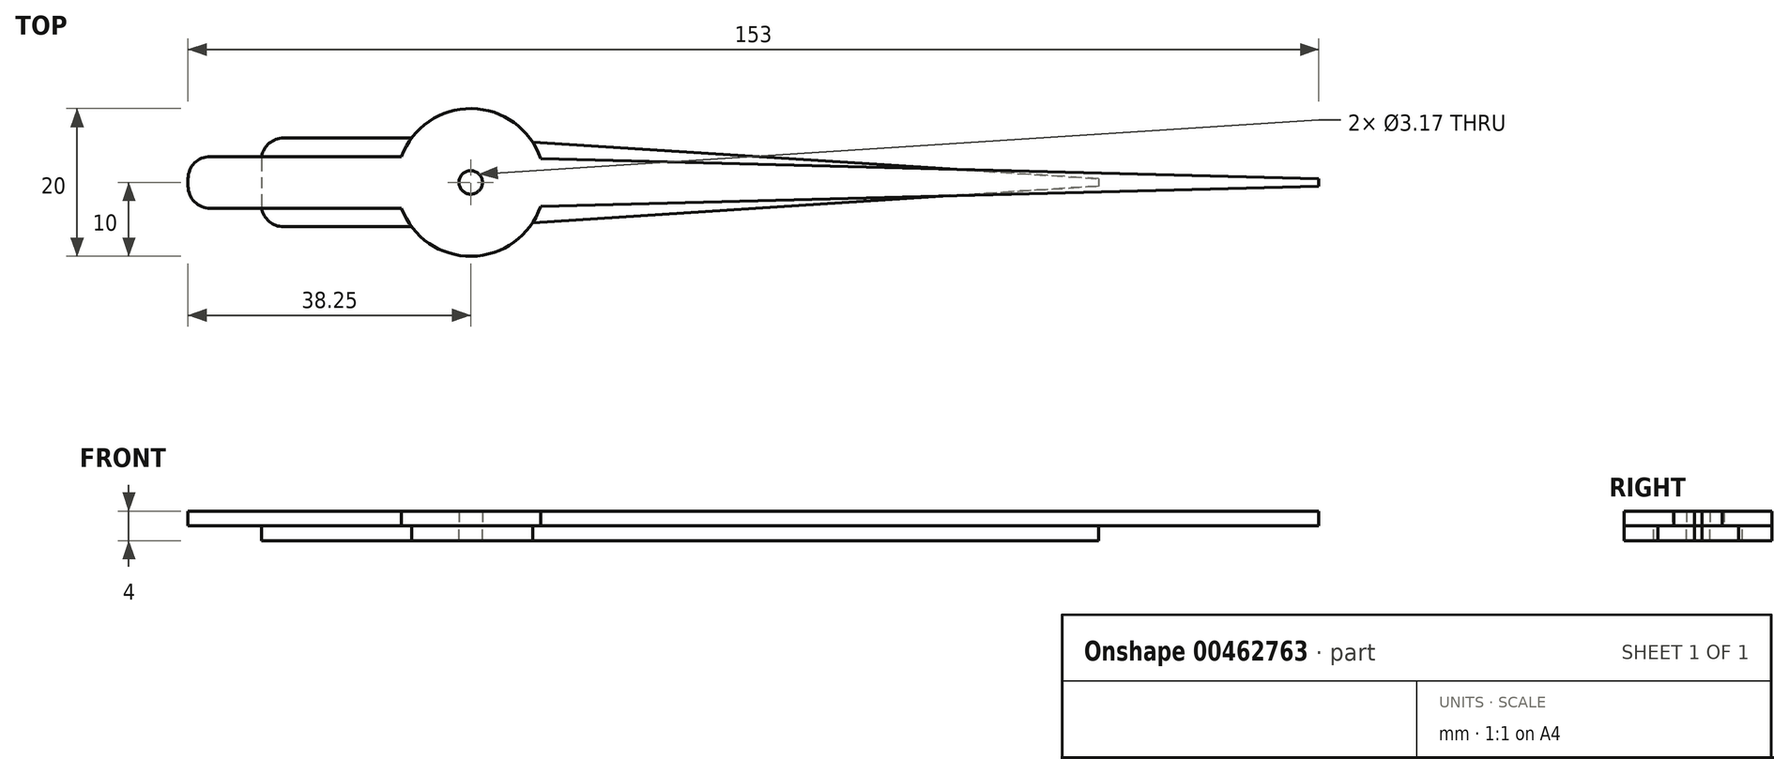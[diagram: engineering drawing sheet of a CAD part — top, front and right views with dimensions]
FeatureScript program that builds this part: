
annotation { "Feature Type Name" : "Feature", "Feature Type Description" : "" }
export const myFeature = defineFeature(function(context is Context, id is Id, definition is map)
    precondition{}
    {
        {
            assignVariable(context, id + "F0", {"name" : "hourLength", "anyValue" : 85 * mm});
        }
        {
            assignVariable(context, id + "F1", {"name" : "minLength", "anyValue" : getVariable(context, 'hourLength') * 1.35});
        }
        {
            assignVariable(context, id + "F2", {"name" : "minWidth", "anyValue" : 7 * mm});
        }
        {
            assignVariable(context, id + "F3", {"name" : "hourWidth", "anyValue" : 12 * mm});
        }
        {
            var Q0;
            Q0=qCreatedBy(makeId("Top.planeOp"),FACE);
            var sketch = newSketch(context, id + "F4", { "sketchPlane" : qUnion([Q0])});
            skCircle(sketch, "E0", {"center": v(0, 0) * mm, "radius": 1.59 * mm});
            skLineSegment(sketch, "E1.bottom", {"start": v(-38.25, 3.5) * mm, "end": v(114.75, 3.5) * mm});
            skLineSegment(sketch, "E1.top", {"start": v(-38.25, -3.5) * mm, "end": v(114.75, -3.5) * mm});
            skLineSegment(sketch, "E1.left", {"start": v(-38.25, 3.5) * mm, "end": v(-38.25, -3.5) * mm});
            skLineSegment(sketch, "E1.right", {"start": v(114.75, 3.5) * mm, "end": v(114.75, -3.5) * mm});
            skCircle(sketch, "E2", {"center": v(0, 0) * mm, "radius": 10 * mm});
            skSolve(sketch);
        }
        {
            var Q0;
            Q0=qSketchRegion(id+"F4",true);
            extrude(context, id + "F5", {"entities" : qUnion([Q0]), "depth" : 2 * mm});
        }
        {
            var Q0;
            Q0=qCreatedBy(makeId("Top.planeOp"),FACE);
            var sketch = newSketch(context, id + "F6", { "sketchPlane" : qUnion([Q0])});
            skCircle(sketch, "E3", {"center": v(0, 0) * mm, "radius": 1.59 * mm});
            skLineSegment(sketch, "E4.bottom", {"start": v(-28.33, 6) * mm, "end": v(85, 6) * mm});
            skLineSegment(sketch, "E4.top", {"start": v(-28.33, -6) * mm, "end": v(85, -6) * mm});
            skLineSegment(sketch, "E4.left", {"start": v(-28.33, 6) * mm, "end": v(-28.33, -6) * mm});
            skLineSegment(sketch, "E4.right", {"start": v(85, 6) * mm, "end": v(85, -6) * mm});
            skCircle(sketch, "E5", {"center": v(0, 0) * mm, "radius": 10 * mm});
            skSolve(sketch);
        }
        {
            var Q0;
            Q0=qSketchRegion(id+"F6",true);
            extrude(context, id + "F7", {"entities" : qUnion([Q0]), "oppositeDirection" : true, "depth" : 2 * mm});
        }
        {
            var Q0;
            Q0=makeQuery(id+"F7.opExtrude","SWEPT_EDGE",EDGE,{"disambiguationData":[OSD([sQuery(id+"F6.wireOp",EDGE,"E4.top"),sQuery(id+"F6.wireOp",EDGE,"E4.right")])]});
            var Q1;
            Q1=makeQuery(id+"F7.opExtrude","SWEPT_EDGE",EDGE,{"disambiguationData":[OSD([sQuery(id+"F6.wireOp",EDGE,"E4.bottom"),sQuery(id+"F6.wireOp",EDGE,"E4.right")])]});
            chamfer(context, id + "F8", {"entities" : qUnion([Q0, Q1]), "chamferType" : ChamferType.TWO_OFFSETS, "width1" : getVariable(context, 'hourLength'), "oppositeDirection" : false, "width2" : getVariable(context, 'hourWidth') / 2 - 0.5 * mm, "tangentPropagation" : true});
        }
        {
            var Q0;
            Q0=makeQuery(id+"F5.opExtrude","SWEPT_EDGE",EDGE,{"disambiguationData":[OSD([sQuery(id+"F4.wireOp",EDGE,"E1.top"),sQuery(id+"F4.wireOp",EDGE,"E1.right")])]});
            var Q1;
            Q1=makeQuery(id+"F5.opExtrude","SWEPT_EDGE",EDGE,{"disambiguationData":[OSD([sQuery(id+"F4.wireOp",EDGE,"E1.bottom"),sQuery(id+"F4.wireOp",EDGE,"E1.right")])]});
            chamfer(context, id + "F9", {"entities" : qUnion([Q0, Q1]), "chamferType" : ChamferType.TWO_OFFSETS, "width1" : getVariable(context, 'minLength'), "oppositeDirection" : true, "width2" : getVariable(context, 'minWidth') / 2 - 0.5 * mm, "tangentPropagation" : true});
        }
        {
            var Q0;
            Q0=makeQuery(id+"F7.opExtrude","SWEPT_EDGE",EDGE,{"disambiguationData":[OSD([sQuery(id+"F6.wireOp",EDGE,"E4.bottom"),sQuery(id+"F6.wireOp",EDGE,"E4.left")])]});
            var Q1;
            Q1=makeQuery(id+"F7.opExtrude","SWEPT_EDGE",EDGE,{"disambiguationData":[OSD([sQuery(id+"F6.wireOp",EDGE,"E4.top"),sQuery(id+"F6.wireOp",EDGE,"E4.left")])]});
            var Q2;
            Q2=makeQuery(id+"F5.opExtrude","SWEPT_EDGE",EDGE,{"disambiguationData":[OSD([sQuery(id+"F4.wireOp",EDGE,"E1.bottom"),sQuery(id+"F4.wireOp",EDGE,"E1.left")])]});
            var Q3;
            Q3=makeQuery(id+"F5.opExtrude","SWEPT_EDGE",EDGE,{"disambiguationData":[OSD([sQuery(id+"F4.wireOp",EDGE,"E1.top"),sQuery(id+"F4.wireOp",EDGE,"E1.left")])]});
            fillet(context, id + "F10", {"entities" : qUnion([Q0, Q1, Q2, Q3]), "radius" : 3 * mm, "tangentPropagation" : true, "allowEdgeOverflow" : false});
        }
    });
